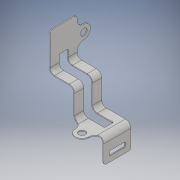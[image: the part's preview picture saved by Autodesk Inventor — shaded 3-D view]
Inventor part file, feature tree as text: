
AUTODESK INVENTOR PART (.ipt)
format: ipt  version: 2019 (Build 230136000, 136)  size: 293,888 bytes
history: native  units: in
note: dims shown in document units (in); Inventor stores cm internally (conversion verified against a paired STEP export)
features: sketch x6, sheet_metal_op x5, chamfer x2, other x2
ambient origin geometry x8: Origin, YZ Plane, XZ Plane, XY Plane, X Axis, Y Axis, Z Axis, Center Point
bodies: Solid1 (feature_tree)
feature tree (15):
  sheet_metal_op  "Face1"
  sheet_metal_op  "Fold1"
  sheet_metal_op  "Fold2"
  sheet_metal_op  "Fold3"
  sheet_metal_op  "Fold4"
  chamfer  "Corner Round1"
  chamfer  "Corner Round2"
  sketch  "Sketch1"  dims[d0=15.0in]
  other  "Plate1"
  sketch  "Sketch2"  dims[d1=3.0in]
  sketch  "Sketch3"  dims[d2=1.5in]
  sketch  "Sketch4"  dims[d3=0.75in]
  sketch  "Sketch5"  dims[d4=2.0in]
  sketch  "Sketch6"  dims[d5=2.0in d6=0.75in d7=1.5in d8=4.0in d9=1.5in d10=1.5in d11=1.5in d12=1.5in d13=0.5in d14=0.6in d15=1.75in d16=0.625in d17=1.0in d18=1.0in d19=9.0in d20=0.1in d21=4.0in d22=0.1in d23=0.05in d24=0.2in d25=0.1in d26=90.0deg d27=0.5in d28=2.5in d29=3.0in d30=3.0in d31=0.1in d32=0.05in d33=0.2in d34=0.1in d35=90.0deg d36=0.5in d37=5.5in d38=2.5in d39=0.1in d40=0.05in d41=0.2in d42=0.1in d43=90.0deg d44=0.5in d45=2.5in d46=0.1in d47=0.05in d48=0.2in d49=0.1in d50=90.0deg d51=0.5in d52=0.5in d53=1.75in d54=0.6in d55=0.625in d56=0.1in d57=0.0in d58=0.1in d59=0.25in]
  other  "Cut1"
